# Revit family: Lighting_Outside_Zero_City_Wire
name_source: partatom
category: Lighting Fixtures
revit_build: Autodesk Revit 2018 (Build: 20190510_1515(x64)
units: mm (PartAtom-declared; Revit-internal decimal feet)

## family parameters
Always vertical = Yes
Cut with Voids When Loaded = No
Light Source = Yes
OmniClass Number = 23.80.70.00
OmniClass Title = Lighting
Part Type = Normal
Room Calculation Point = No
Round Connector Dimension = Use Diameter
Shared = No
Work Plane-Based = No

## types (12) — shared parameters
AssetType = Fixed
BIMObjectName = Lighting_Outside_Zero_City_Wire
Brand = Zero
Collection = City
Color = Various
Color Filter = 16777215
Constituents = Glass diffuser
Description = City has a wide range of applications: outdoor or indoor, enhancing retail environments, industries and public transport.
Designer = Thomas Bernstrand
Dimming Lamp Color Temperature Shift = <None>
DurationUnit = Year
Features = Terminal block inside housing. Conduit entry
Finish = Painted aluminum
HasProtectiveEarth = No
IP_Code = IP 20
IfcExportAs = IfcLightFixtureType
IfcExportType = NOTDEFINED
LightFixtureMountingType = Suspended
LightFixturePlacingType = Other
Manufacturer = Zero
ManufacturerName = Zero
ManufacturerURL = https://www.zerolighting.com
Material = Metal
NBSDescription = General purpose luminaires
NBSReference = 90-60-50/405
Name = Zero_City_Wire
NominalDiameter = 555 mm  [stored 1.82087 ft]
NominalFrequencyRange = 50 Hz
NominalRadius = 278 mm
NominalVoltage = 230 V
NominalVoltageCalc = 0 V
Nominal_Height = 521 mm
Nominal_Length = 554 mm
Nominal_Width = 554 mm
NumberOfPoles = 1
ProductDatasheet = https://www.zerolighting.com
ProductInformation = City has a wide range of applications: outdoor or indoor, enhancing retail environments, industries and public transport.
Revision = 6
Shape = Cone
Size = 555x555x428 mm
Tilt Angle = 90.00°
URL = https://www.zerolighting.com
Uniclass2 = Pr_70_70_49_86
Uniclass2015Description = Suspended luminaires
Uniclass2015Reference = Pr_70_70_48_86
Version = 2
VersionDate = 16/12/2021
WarrantyDurationUnit = Year
zero-valued in all types: DefaultElevation, NumberOfSources

## per-type parameters (varying)
| type | ArticleNumber | Category | ElectricalDeviceNominalPower | LightFixtureMainMaterial | ModelNumber | Photometric Web File | TotalWattage |
| City wire catenary - 2120LM/32W Black On/Off | 12081306-30 | Luminaires | 32 | Black RAL 9005 | 12081306-30 | City120813.IES | 32 W |
| City wire catenary - 2120LM/32W Black Dali | 12081306D30 | Wire | 32 | Black RAL 9005 | 12081306D30 | City120813.IES | 32 W |
| City wire catenary - 2120LM/32W Beige Grey On/Off | 12081366-30 | Wire | 32 | Beige Grey RAL 7006 | 12081366-30 | City120813.IES | 32 W |
| City wire catenary - 2120LM/32W Beige Grey Dali | 12081366D30 | Wire | 32 | Beige Grey RAL 7006 | 12081366D30 | City120813.IES | 32 W |
| City wire catenary - 2120LM/32W Beige Grey Night | 12081366N30 | Wire | 32 | Beige Grey RAL 7006 | 12081366N30 | City120813.IES | 32 W |
| City wire catenary - 2120LM/32W Black Night | 12081306N30 | Wire | 32 | Black RAL 9005 | 12081306N30 | City120813.IES | 32 W |
| City wire catenary - 1660LM/18W Beige Grey Dali | 12080366D30 | Wire | 18 | Beige Grey RAL 7006 | 12080366D30 | City120803.IES | 18 W |
| City wire catenary - 1660LM/18W Beige Grey Night | 12080366N30 | Wire | 18 | Beige Grey RAL 7006 | 12080366N30 | City120803.IES | 18 W |
| City wire catenary - 1660LM/18W Beige Grey On/Off | 12080366-30 | Wire | 18 | Beige Grey RAL 7006 | 12080366-30 | City120803.IES | 18 W |
| City wire catenary - 1660LM/18W Black Dali | 12080306D30 | Wire | 18 | Black RAL 9005 | 12080306D30 | City120803.IES | 18 W |
| City wire catenary - 1660LM/18W Black Night | 12080306N30 | Wire | 18 | Black RAL 9005 | 12080306N30 | City120803.IES | 18 W |
| City wire catenary - 1660LM/18W Black On/Off | 12080306-30 | Wire | 18 | Black RAL 9005 | 12080306-30 | City120803.IES | 18 W |

note: column(s) folded — value = type name in every type: Model

note: [stored X ft] marks values corroborated as IEEE doubles in the binary element streams (Revit-internal decimal feet)

## geometry (parser evidence)
native form markers: Sweep x6
no freeform markers — native parametric forms only
